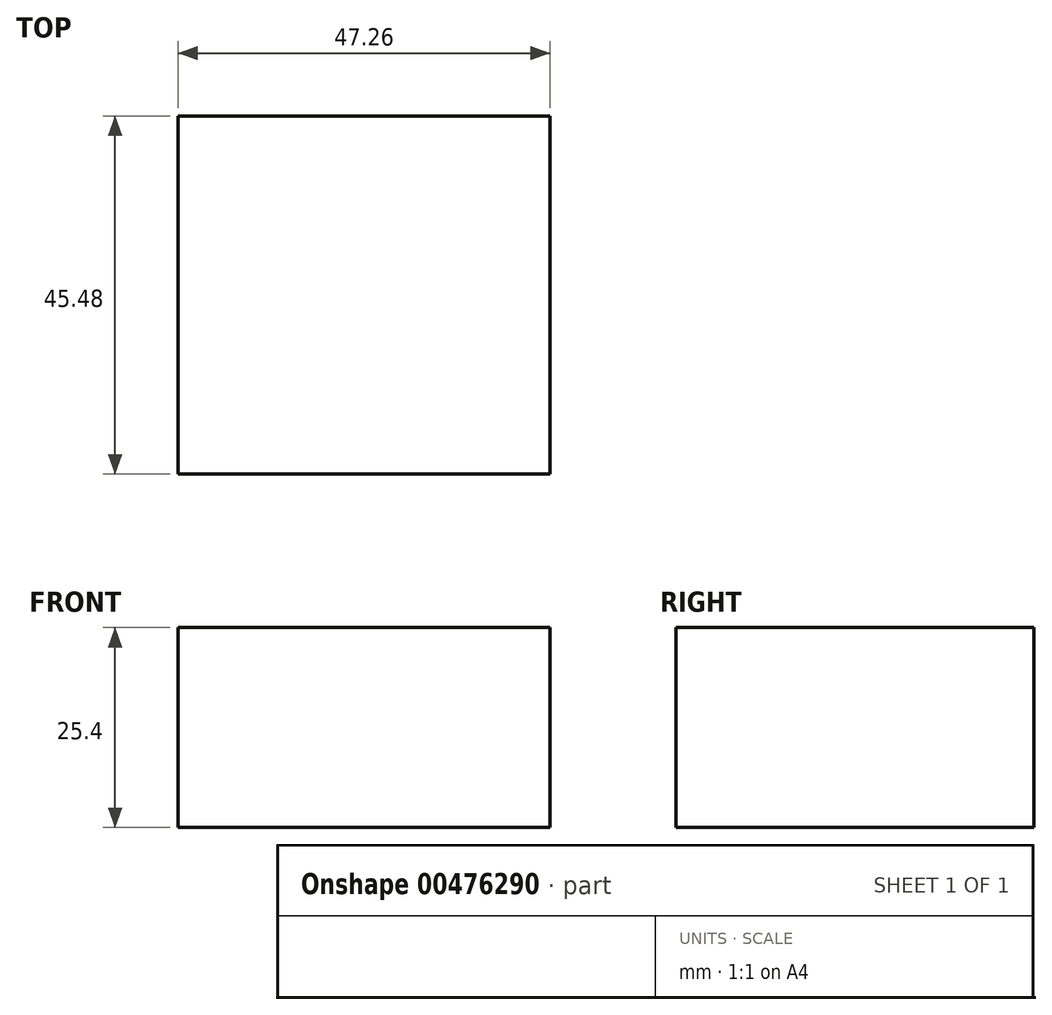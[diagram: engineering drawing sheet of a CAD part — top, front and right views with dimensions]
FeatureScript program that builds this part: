
annotation { "Feature Type Name" : "Feature", "Feature Type Description" : "" }
export const myFeature = defineFeature(function(context is Context, id is Id, definition is map)
    precondition{}
    {
        {
            var Q0;
            Q0=qCreatedBy(makeId("Top.planeOp"),FACE);
            var sketch = newSketch(context, id + "F0", { "sketchPlane" : qUnion([Q0])});
            skLineSegment(sketch, "E0.bottom", {"start": v(23.63, -22.74) * mm, "end": v(-23.63, -22.74) * mm});
            skLineSegment(sketch, "E0.top", {"start": v(23.63, 22.74) * mm, "end": v(-23.63, 22.74) * mm});
            skLineSegment(sketch, "E0.left", {"start": v(23.63, -22.74) * mm, "end": v(23.63, 22.74) * mm});
            skLineSegment(sketch, "E0.right", {"start": v(-23.63, -22.74) * mm, "end": v(-23.63, 22.74) * mm});
            skPoint(sketch, "E0.middle", {"position": v(0, 0) * mm});
            skSolve(sketch);
        }
        {
            var Q0;
            Q0=makeQuery(id+"F0.imprint","IMPRINT",FACE,{"disambiguationData":[TD([[makeQuery(id+"F0.imprint","IMPRINT",EDGE,{"derivedFrom":sQuery(id+"F0.wireOp",EDGE,"E0.bottom")}),-1.0]])]});
            extrude(context, id + "F1", {"entities" : qUnion([Q0]), "depth" : 25.4 * mm});
        }
    });
